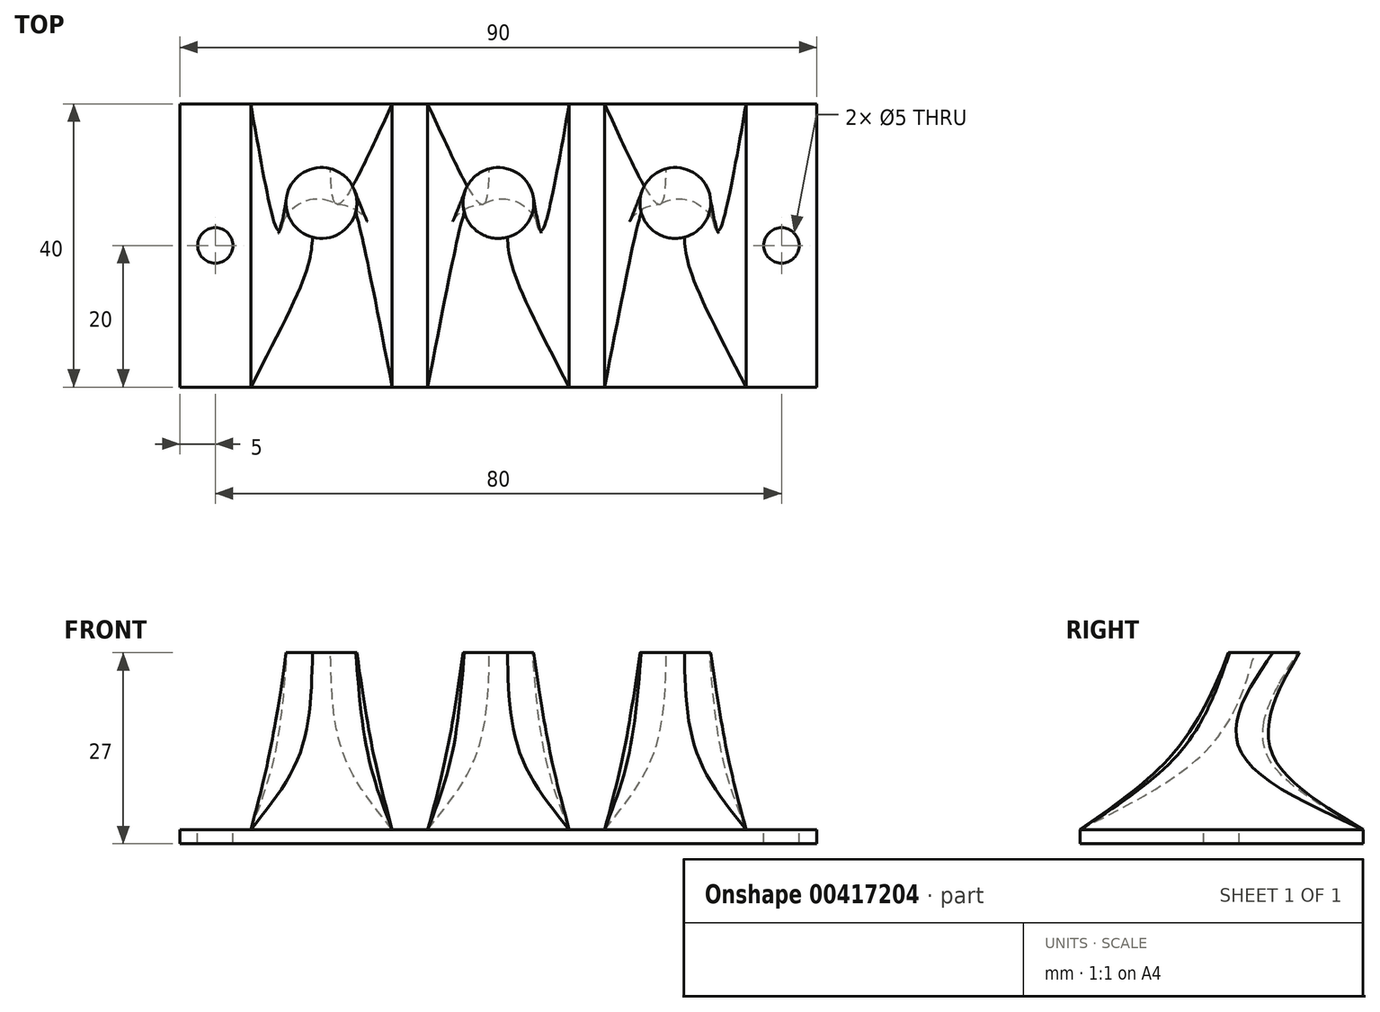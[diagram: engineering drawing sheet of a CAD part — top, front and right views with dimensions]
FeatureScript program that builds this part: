
annotation { "Feature Type Name" : "Feature", "Feature Type Description" : "" }
export const myFeature = defineFeature(function(context is Context, id is Id, definition is map)
    precondition{}
    {
        {
            var Q0;
            Q0=qCreatedBy(makeId("Top.planeOp"),FACE);
            var sketch = newSketch(context, id + "F0", { "sketchPlane" : qUnion([Q0])});
            skLineSegment(sketch, "E0.bottom", {"start": v(10, -20) * mm, "end": v(-10, -20) * mm});
            skLineSegment(sketch, "E0.top", {"start": v(10, 20) * mm, "end": v(-10, 20) * mm});
            skLineSegment(sketch, "E0.left", {"start": v(10, -20) * mm, "end": v(10, 20) * mm});
            skLineSegment(sketch, "E0.right", {"start": v(-10, -20) * mm, "end": v(-10, 20) * mm});
            skPoint(sketch, "E0.middle", {"position": v(0, 0) * mm});
            skSolve(sketch);
        }
        {
            var Q0;
            Q0=qCreatedBy(makeId("Top.planeOp"),FACE);
            cPlane(context, id + "F1", {"entities" : qUnion([Q0]), "cplaneType" : CPlaneType.OFFSET, "offset" : 25 * mm, "width" : 150 * mm, "height" : 150 * mm});
        }
        {
            var Q0;
            Q0=qCreatedBy(id+"F1.planeOp",FACE);
            var sketch = newSketch(context, id + "F2", { "sketchPlane" : qUnion([Q0])});
            skCircle(sketch, "E1", {"center": v(0, 6) * mm, "radius": 5 * mm});
            skSolve(sketch);
        }
        {
            var Q0;
            Q0=qCreatedBy(makeId("Top.planeOp"),FACE);
            cPlane(context, id + "F3", {"entities" : qUnion([Q0]), "cplaneType" : CPlaneType.OFFSET, "offset" : 10 * mm, "width" : 150 * mm, "height" : 150 * mm});
        }
        {
            var Q0;
            Q0=qCreatedBy(id+"F3.planeOp",FACE);
            var sketch = newSketch(context, id + "F4", { "sketchPlane" : qUnion([Q0])});
            skCircle(sketch, "E2", {"center": v(0, 0) * mm, "radius": 7.5 * mm});
            skSolve(sketch);
        }
        {
            var Q0;
            Q0=makeQuery(id+"F0.imprint","IMPRINT",FACE,{"disambiguationData":[TD([[makeQuery(id+"F0.imprint","IMPRINT",EDGE,{"derivedFrom":sQuery(id+"F0.wireOp",EDGE,"E0.bottom")}),-1.0]])]});
            var Q1;
            Q1=makeQuery(id+"F4.imprint","IMPRINT",FACE,{"disambiguationData":[TD([[makeQuery(id+"F4.imprint","IMPRINT",EDGE,{"derivedFrom":sQuery(id+"F4.wireOp",EDGE,"E2")}),1.0]])]});
            var Q2;
            Q2=makeQuery(id+"F2.imprint","IMPRINT",FACE,{"disambiguationData":[TD([[makeQuery(id+"F2.imprint","IMPRINT",EDGE,{"derivedFrom":sQuery(id+"F2.wireOp",EDGE,"E1")}),1.0]])]});
            loft(context, id + "F5", {"sheetProfilesArray" : [{ "sheetProfileEntities" : qUnion([Q0]) }, { "sheetProfileEntities" : qUnion([Q1]) }, { "sheetProfileEntities" : qUnion([Q2]) }]});
        }
        {
            var Q0;
            Q0=qCreatedBy(makeId("Top.planeOp"),FACE);
            var sketch = newSketch(context, id + "F6", { "sketchPlane" : qUnion([Q0])});
            skLineSegment(sketch, "E3", {"start": v(0, 0) * mm, "end": v(25, 0) * mm});
            skLineSegment(sketch, "E4.bottom", {"start": v(35, -20) * mm, "end": v(15, -20) * mm});
            skLineSegment(sketch, "E4.top", {"start": v(35, 20) * mm, "end": v(15, 20) * mm});
            skLineSegment(sketch, "E4.left", {"start": v(35, -20) * mm, "end": v(35, 20) * mm});
            skLineSegment(sketch, "E4.right", {"start": v(15, -20) * mm, "end": v(15, 20) * mm});
            skPoint(sketch, "E4.middle", {"position": v(25, 0) * mm});
            skSolve(sketch);
        }
        {
            var Q0;
            Q0=qCreatedBy(makeId("Top.planeOp"),FACE);
            cPlane(context, id + "F7", {"entities" : qUnion([Q0]), "cplaneType" : CPlaneType.OFFSET, "offset" : 10 * mm, "width" : 150 * mm, "height" : 150 * mm});
        }
        {
            var Q0;
            Q0=qCreatedBy(id+"F7.planeOp",FACE);
            var sketch = newSketch(context, id + "F8", { "sketchPlane" : qUnion([Q0])});
            skLineSegment(sketch, "E5", {"start": v(0, 0) * mm, "end": v(25, 0) * mm});
            skCircle(sketch, "E6", {"center": v(25, 0) * mm, "radius": 7.5 * mm});
            skSolve(sketch);
        }
        {
            var Q0;
            Q0=qCreatedBy(makeId("Top.planeOp"),FACE);
            cPlane(context, id + "F9", {"entities" : qUnion([Q0]), "cplaneType" : CPlaneType.OFFSET, "offset" : 25 * mm, "width" : 150 * mm, "height" : 150 * mm});
        }
        {
            var Q0;
            Q0=qCreatedBy(id+"F9.planeOp",FACE);
            var sketch = newSketch(context, id + "F10", { "sketchPlane" : qUnion([Q0])});
            skLineSegment(sketch, "E7", {"start": v(0, 0) * mm, "end": v(25, 0) * mm});
            skLineSegment(sketch, "E8", {"start": v(25, 0) * mm, "end": v(25, 6) * mm});
            skCircle(sketch, "E9", {"center": v(25, 6) * mm, "radius": 5 * mm});
            skSolve(sketch);
        }
        {
            var Q0;
            {var subQ0=sQuery(id+"F6.wireOp",EDGE,"E4.bottom");Q0=makeQuery(id+"F6.imprint","IMPRINT",FACE,{"disambiguationData":[TD([[makeQuery(id+"F6.imprint","IMPRINT",EDGE,{"derivedFrom":subQ0}),-1.0]])]});}
            var Q1;
            Q1=makeQuery(id+"F8.imprint","IMPRINT",FACE,{"disambiguationData":[TD([[makeQuery(id+"F8.imprint","IMPRINT",EDGE,{"derivedFrom":sQuery(id+"F8.wireOp",EDGE,"E6")}),1.0]])]});
            var Q2;
            Q2=makeQuery(id+"F10.imprint","IMPRINT",FACE,{"disambiguationData":[TD([[makeQuery(id+"F10.imprint","IMPRINT",EDGE,{"derivedFrom":sQuery(id+"F10.wireOp",EDGE,"E9")}),1.0]])]});
            loft(context, id + "F11", {"sheetProfilesArray" : [{ "sheetProfileEntities" : qUnion([Q0]) }, { "sheetProfileEntities" : qUnion([Q1]) }, { "sheetProfileEntities" : qUnion([Q2]) }]});
        }
        {
            var Q0;
            Q0=qCreatedBy(makeId("Top.planeOp"),FACE);
            var sketch = newSketch(context, id + "F12", { "sketchPlane" : qUnion([Q0])});
            skLineSegment(sketch, "E10", {"start": v(0, 0) * mm, "end": v(-25, 0) * mm});
            skLineSegment(sketch, "E11.bottom", {"start": v(-35, -20) * mm, "end": v(-15, -20) * mm});
            skLineSegment(sketch, "E11.top", {"start": v(-35, 20) * mm, "end": v(-15, 20) * mm});
            skLineSegment(sketch, "E11.left", {"start": v(-35, -20) * mm, "end": v(-35, 20) * mm});
            skLineSegment(sketch, "E11.right", {"start": v(-15, -20) * mm, "end": v(-15, 20) * mm});
            skPoint(sketch, "E11.middle", {"position": v(-25, 0) * mm});
            skSolve(sketch);
        }
        {
            var Q0;
            Q0=qCreatedBy(makeId("Top.planeOp"),FACE);
            cPlane(context, id + "F13", {"entities" : qUnion([Q0]), "cplaneType" : CPlaneType.OFFSET, "offset" : 10 * mm, "width" : 150 * mm, "height" : 150 * mm});
        }
        {
            var Q0;
            Q0=qCreatedBy(id+"F13.planeOp",FACE);
            var sketch = newSketch(context, id + "F14", { "sketchPlane" : qUnion([Q0])});
            skLineSegment(sketch, "E12", {"start": v(0, 0) * mm, "end": v(-25, 0) * mm});
            skCircle(sketch, "E13", {"center": v(-25, 0) * mm, "radius": 7.5 * mm});
            skSolve(sketch);
        }
        {
            var Q0;
            Q0=qCreatedBy(makeId("Top.planeOp"),FACE);
            cPlane(context, id + "F15", {"entities" : qUnion([Q0]), "cplaneType" : CPlaneType.OFFSET, "offset" : 25 * mm, "width" : 150 * mm, "height" : 150 * mm});
        }
        {
            var Q0;
            Q0=qCreatedBy(id+"F15.planeOp",FACE);
            var sketch = newSketch(context, id + "F16", { "sketchPlane" : qUnion([Q0])});
            skLineSegment(sketch, "E14", {"start": v(0, 0) * mm, "end": v(-25, 0) * mm});
            skLineSegment(sketch, "E15", {"start": v(-25, 0) * mm, "end": v(-25, 6) * mm});
            skCircle(sketch, "E16", {"center": v(-25, 6) * mm, "radius": 5 * mm});
            skSolve(sketch);
        }
        {
            var Q0;
            {var subQ0=sQuery(id+"F12.wireOp",EDGE,"E11.bottom");Q0=makeQuery(id+"F12.imprint","IMPRINT",FACE,{"disambiguationData":[TD([[makeQuery(id+"F12.imprint","IMPRINT",EDGE,{"derivedFrom":subQ0}),1.0]])]});}
            var Q1;
            Q1=makeQuery(id+"F14.imprint","IMPRINT",FACE,{"disambiguationData":[TD([[makeQuery(id+"F14.imprint","IMPRINT",EDGE,{"derivedFrom":sQuery(id+"F14.wireOp",EDGE,"E13")}),1.0]])]});
            var Q2;
            Q2=makeQuery(id+"F16.imprint","IMPRINT",FACE,{"disambiguationData":[TD([[makeQuery(id+"F16.imprint","IMPRINT",EDGE,{"derivedFrom":sQuery(id+"F16.wireOp",EDGE,"E16")}),1.0]])]});
            loft(context, id + "F17", {"sheetProfilesArray" : [{ "sheetProfileEntities" : qUnion([Q0]) }, { "sheetProfileEntities" : qUnion([Q1]) }, { "sheetProfileEntities" : qUnion([Q2]) }]});
        }
        {
            var Q0;
            Q0=qCreatedBy(makeId("Top.planeOp"),FACE);
            var sketch = newSketch(context, id + "F18", { "sketchPlane" : qUnion([Q0])});
            skLineSegment(sketch, "E17.bottom", {"start": v(45, -20) * mm, "end": v(-45, -20) * mm});
            skLineSegment(sketch, "E17.top", {"start": v(45, 20) * mm, "end": v(-45, 20) * mm});
            skLineSegment(sketch, "E17.left", {"start": v(45, -20) * mm, "end": v(45, 20) * mm});
            skLineSegment(sketch, "E17.right", {"start": v(-45, -20) * mm, "end": v(-45, 20) * mm});
            skPoint(sketch, "E17.middle", {"position": v(0, 0) * mm});
            skSolve(sketch);
        }
        {
            var Q0;
            Q0 = qSketchRegion(id + "F18", true);
            extrude(context, id + "F19", {"entities" : qUnion([Q0]), "oppositeDirection" : true, "depth" : 2 * mm, "offsetDistance" : 25 * mm});
        }
        {
            var Q0;
            Q0=makeQuery(id+"F19.opExtrude","CAP_FACE",FACE,{"disambiguationData":[OSD([sQuery(id+"F18.wireOp",EDGE,"E17.bottom"),sQuery(id+"F18.wireOp",EDGE,"E17.top"),sQuery(id+"F18.wireOp",EDGE,"E17.left"),sQuery(id+"F18.wireOp",EDGE,"E17.right")])],"isStart":true});
            var sketch = newSketch(context, id + "F20", { "sketchPlane" : qUnion([Q0])});
            skLineSegment(sketch, "E18", {"start": v(45, 0) * mm, "end": v(40, 0) * mm});
            skLineSegment(sketch, "E19", {"start": v(-45, 0) * mm, "end": v(-40, 0) * mm});
            skSolve(sketch);
        }
        {
            var Q0;
            Q0=sQuery(id+"F20.wireOp",VERTEX,"E18.end");
            var Q1;
            Q1=sQuery(id+"F20.wireOp",VERTEX,"E19.end");
            var Q2;
            Q2=makeQuery(id+"F19.opExtrude","SWEPT_BODY",BODY,{"disambiguationData":[OSD([sQuery(id+"F18.wireOp",EDGE,"E17.bottom"),sQuery(id+"F18.wireOp",EDGE,"E17.top"),sQuery(id+"F18.wireOp",EDGE,"E17.left"),sQuery(id+"F18.wireOp",EDGE,"E17.right")])]});
            hole(context, id + "F21", {"style" : HoleStyle.C_BORE, "endStyle" : HoleEndStyle.BLIND, "holeDiameter" : 5 * mm, "cBoreDiameter" : 5 * mm, "cBoreDepth" : 2 * mm, "holeDepth" : 8 * mm, "isTappedThrough" : true, "tappedDepth" : 12 * mm, "tapClearance" : 3, "locations" : qUnion([Q0, Q1]), "scope" : qUnion([Q2])});
        }
    });
